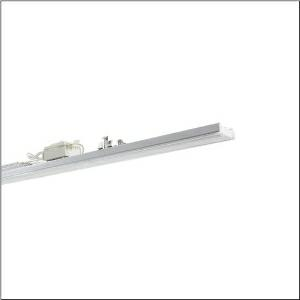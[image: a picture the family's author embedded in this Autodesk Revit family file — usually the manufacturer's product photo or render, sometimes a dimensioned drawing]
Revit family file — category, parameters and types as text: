
# Revit family: licross_r__21_recessed_ho_52te11dv4lxs_d195
name_source: partatom
category: Lighting Fixtures
units: mm (PartAtom-declared; Revit-internal decimal feet)

## family parameters
Cut with Voids When Loaded = No
Host = Face
Light Source = No
Part Type = Normal
Room Calculation Point = No
Round Connector Dimension = Use Diameter
Shared = No

## types (1)
- --- (1 x LED, 20000 lm, 110.1 W, 4000K)
    Apparent Load = 110 VA
    CIE Flux Codes = 87 95 99 100 100
    Color Rendering = 80
    Color Temperature = 4000K
    Default Elevation = 1800 mm
    Description = Licross® 21 Recessed HO, luminaire insert, of sheet steel, galvanised, coil coated, white, length: 2.250mm, width: 66mm, height: 67mm, LED rated luminous flux: 20.000lm, light colour: 840, control gear: DALI 2, with plug, 5-pole, with phase selection, mains connection: 220..240V, AC, 50/60Hz, rated input power: 110W, halogen-free wiring, primary light control with lens, of plastic, primary optical cover: cover, of PMMA, light emission: direct distribution, primary light characteristic: symmetric, protection rating (complete): IP54, insulation class (complete): insulation class I (protective earthing), certification: CE, ENEC, VDE, UKCA, protection symbol: D if used in an environment with non-conductive dust loads with corresponding accessories, impact resistance: IK06, permissible ambient temperature for indoor applications: -40..+35°C, corresponds to IFS (International Featured Standards) requirements for safety and quality in the food industry, reducing of maximum allowable ambient temperature of 5°C with ceiling mounting, LABS conformity tested according to VDMA 24364:2018-05, packaging unit: 1 piece
    Height = 58 mm
    Lamp = 1 x LED
    Lamp Light Flux = 20000 lm
    Lamp Power = 110.1 W
    Lamp count = 1
    Length = 2250 mm
    Luminous efficacy = 182 lm/W
    Manufacturer = Siteco
    ModVariant = No
    Model = 52TE11DV4LXS
    Mounting Place = Ceiling
    Mounting Type = Pendant
    Number of Poles = 1
    OnlyDefault = Yes
    Power Factor = 1
    Product Name = Licross® 21 Recessed HO
    Product group = luminaire insert
    ProductGroupID = 902
    Protection Class = Protection class I
    Protection Degree = IP 54
    RLX_Detail_Level = 1
    RLX_Emergency_Light_Flux = 0 lm
    RLX_Emergency_Type = 0
    RLX_Emergency_Type_DB = No
    RlxData = <blob elided: 29449 chars, md5=f14982aa>
    Socket = socket
    Standby Power = 0 W
    System Light Flux = 20000 lm
    System Power = 110 W
    Type Comments = factory setting: luminous flux: 100 % | dim-lin: 254 | 426 mA
    Type Image = l_1296930.jpg
    URL = http://relux.com
    VarID = @adj_127336
    Voltage = 0 V
    Weight = 0.00 kg
    Width = 66 mm

## geometry (parser evidence)
native form markers: Blend x4, Sweep x10
no freeform markers — native parametric forms only
